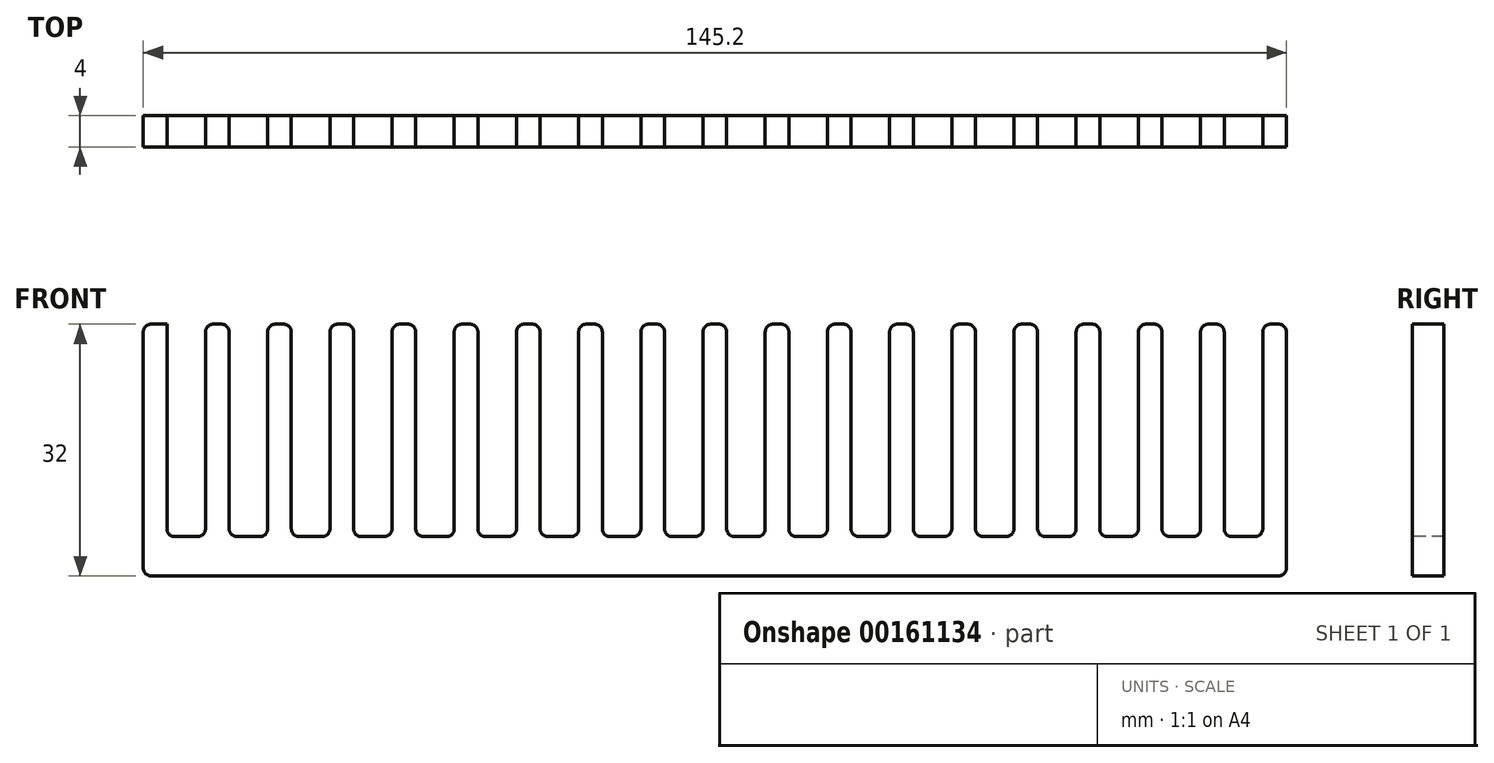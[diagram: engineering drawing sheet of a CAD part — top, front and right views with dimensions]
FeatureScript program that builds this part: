
annotation { "Feature Type Name" : "Feature", "Feature Type Description" : "" }
export const myFeature = defineFeature(function(context is Context, id is Id, definition is map)
    precondition{}
    {
        {
            var Q0;
            Q0=qCreatedBy(makeId("Front.planeOp"),FACE);
            var sketch = newSketch(context, id + "F0", { "sketchPlane" : qUnion([Q0])});
            skLineSegment(sketch, "E0.bottom", {"start": v(2.45, 13.5) * mm, "end": v(-2.45, 13.5) * mm});
            skLineSegment(sketch, "E0.top", {"start": v(1.45, -13.5) * mm, "end": v(-1.45, -13.5) * mm});
            skLineSegment(sketch, "E0.left", {"start": v(2.45, 13.5) * mm, "end": v(2.45, -12.5) * mm});
            skLineSegment(sketch, "E0.right", {"start": v(-2.45, 13.5) * mm, "end": v(-2.45, -12.5) * mm});
            skPoint(sketch, "E0.middle", {"position": v(0, 0) * mm});
            skPoint(sketch, "E1.visualSharp", {"position": v(-2.45, -13.5) * mm});
            skArc(sketch, "E1.filletArc", {"start": v(-2.45, -12.5) * mm, "mid": v(-2.16, -13.2) * mm, "end": v(-1.45, -13.5) * mm});
            skPoint(sketch, "E2.visualSharp", {"position": v(2.45, -13.5) * mm});
            skArc(sketch, "E2.filletArc", {"start": v(1.45, -13.5) * mm, "mid": v(2.16, -13.2) * mm, "end": v(2.45, -12.5) * mm});
            skLineSegment(sketch, "E3.1.0.0", {"start": v(5.45, 13.5) * mm, "end": v(5.45, -12.5) * mm});
            skLineSegment(sketch, "E3.1.0.1", {"start": v(10.35, 13.5) * mm, "end": v(10.35, -12.5) * mm});
            skLineSegment(sketch, "E3.1.0.2", {"start": v(10.35, 13.5) * mm, "end": v(5.45, 13.5) * mm});
            skPoint(sketch, "E3.1.0.3", {"position": v(5.45, -13.5) * mm});
            skPoint(sketch, "E3.1.0.4", {"position": v(7.9, 0) * mm});
            skPoint(sketch, "E3.1.0.5", {"position": v(10.35, -13.5) * mm});
            skLineSegment(sketch, "E3.1.0.6", {"start": v(9.35, -13.5) * mm, "end": v(6.45, -13.5) * mm});
            skArc(sketch, "E3.1.0.7", {"start": v(5.45, -12.5) * mm, "mid": v(5.74, -13.2) * mm, "end": v(6.45, -13.5) * mm});
            skArc(sketch, "E3.1.0.8", {"start": v(9.35, -13.5) * mm, "mid": v(10.06, -13.2) * mm, "end": v(10.35, -12.5) * mm});
            skLineSegment(sketch, "E3.2.0.0", {"start": v(13.35, 13.5) * mm, "end": v(13.35, -12.5) * mm});
            skLineSegment(sketch, "E3.2.0.1", {"start": v(18.25, 13.5) * mm, "end": v(18.25, -12.5) * mm});
            skLineSegment(sketch, "E3.2.0.2", {"start": v(18.25, 13.5) * mm, "end": v(13.35, 13.5) * mm});
            skPoint(sketch, "E3.2.0.3", {"position": v(13.35, -13.5) * mm});
            skPoint(sketch, "E3.2.0.4", {"position": v(15.8, 0) * mm});
            skPoint(sketch, "E3.2.0.5", {"position": v(18.25, -13.5) * mm});
            skLineSegment(sketch, "E3.2.0.6", {"start": v(17.25, -13.5) * mm, "end": v(14.35, -13.5) * mm});
            skArc(sketch, "E3.2.0.7", {"start": v(13.35, -12.5) * mm, "mid": v(13.64, -13.2) * mm, "end": v(14.35, -13.5) * mm});
            skArc(sketch, "E3.2.0.8", {"start": v(17.25, -13.5) * mm, "mid": v(17.96, -13.2) * mm, "end": v(18.25, -12.5) * mm});
            skLineSegment(sketch, "E3.3.0.0", {"start": v(21.25, 13.5) * mm, "end": v(21.25, -12.5) * mm});
            skLineSegment(sketch, "E3.3.0.1", {"start": v(26.15, 13.5) * mm, "end": v(26.15, -12.5) * mm});
            skLineSegment(sketch, "E3.3.0.2", {"start": v(26.15, 13.5) * mm, "end": v(21.25, 13.5) * mm});
            skPoint(sketch, "E3.3.0.3", {"position": v(21.25, -13.5) * mm});
            skPoint(sketch, "E3.3.0.4", {"position": v(23.7, 0) * mm});
            skPoint(sketch, "E3.3.0.5", {"position": v(26.15, -13.5) * mm});
            skLineSegment(sketch, "E3.3.0.6", {"start": v(25.15, -13.5) * mm, "end": v(22.25, -13.5) * mm});
            skArc(sketch, "E3.3.0.7", {"start": v(21.25, -12.5) * mm, "mid": v(21.54, -13.2) * mm, "end": v(22.25, -13.5) * mm});
            skArc(sketch, "E3.3.0.8", {"start": v(25.15, -13.5) * mm, "mid": v(25.86, -13.2) * mm, "end": v(26.15, -12.5) * mm});
            skLineSegment(sketch, "E3.4.0.0", {"start": v(29.15, 13.5) * mm, "end": v(29.15, -12.5) * mm});
            skLineSegment(sketch, "E3.4.0.1", {"start": v(34.05, 13.5) * mm, "end": v(34.05, -12.5) * mm});
            skLineSegment(sketch, "E3.4.0.2", {"start": v(34.05, 13.5) * mm, "end": v(29.15, 13.5) * mm});
            skPoint(sketch, "E3.4.0.3", {"position": v(29.15, -13.5) * mm});
            skPoint(sketch, "E3.4.0.4", {"position": v(31.6, 0) * mm});
            skPoint(sketch, "E3.4.0.5", {"position": v(34.05, -13.5) * mm});
            skLineSegment(sketch, "E3.4.0.6", {"start": v(33.05, -13.5) * mm, "end": v(30.15, -13.5) * mm});
            skArc(sketch, "E3.4.0.7", {"start": v(29.15, -12.5) * mm, "mid": v(29.44, -13.2) * mm, "end": v(30.15, -13.5) * mm});
            skArc(sketch, "E3.4.0.8", {"start": v(33.05, -13.5) * mm, "mid": v(33.76, -13.2) * mm, "end": v(34.05, -12.5) * mm});
            skLineSegment(sketch, "E3.5.0.0", {"start": v(37.05, 13.5) * mm, "end": v(37.05, -12.5) * mm});
            skLineSegment(sketch, "E3.5.0.1", {"start": v(41.95, 13.5) * mm, "end": v(41.95, -12.5) * mm});
            skLineSegment(sketch, "E3.5.0.2", {"start": v(41.95, 13.5) * mm, "end": v(37.05, 13.5) * mm});
            skPoint(sketch, "E3.5.0.3", {"position": v(37.05, -13.5) * mm});
            skPoint(sketch, "E3.5.0.4", {"position": v(39.5, 0) * mm});
            skPoint(sketch, "E3.5.0.5", {"position": v(41.95, -13.5) * mm});
            skLineSegment(sketch, "E3.5.0.6", {"start": v(40.95, -13.5) * mm, "end": v(38.05, -13.5) * mm});
            skArc(sketch, "E3.5.0.7", {"start": v(37.05, -12.5) * mm, "mid": v(37.34, -13.2) * mm, "end": v(38.05, -13.5) * mm});
            skArc(sketch, "E3.5.0.8", {"start": v(40.95, -13.5) * mm, "mid": v(41.66, -13.2) * mm, "end": v(41.95, -12.5) * mm});
            skLineSegment(sketch, "E3.6.0.0", {"start": v(44.95, 13.5) * mm, "end": v(44.95, -12.5) * mm});
            skLineSegment(sketch, "E3.6.0.1", {"start": v(49.85, 13.5) * mm, "end": v(49.85, -12.5) * mm});
            skLineSegment(sketch, "E3.6.0.2", {"start": v(49.85, 13.5) * mm, "end": v(44.95, 13.5) * mm});
            skPoint(sketch, "E3.6.0.3", {"position": v(44.95, -13.5) * mm});
            skPoint(sketch, "E3.6.0.4", {"position": v(47.4, 0) * mm});
            skPoint(sketch, "E3.6.0.5", {"position": v(49.85, -13.5) * mm});
            skLineSegment(sketch, "E3.6.0.6", {"start": v(48.85, -13.5) * mm, "end": v(45.95, -13.5) * mm});
            skArc(sketch, "E3.6.0.7", {"start": v(44.95, -12.5) * mm, "mid": v(45.24, -13.2) * mm, "end": v(45.95, -13.5) * mm});
            skArc(sketch, "E3.6.0.8", {"start": v(48.85, -13.5) * mm, "mid": v(49.56, -13.2) * mm, "end": v(49.85, -12.5) * mm});
            skLineSegment(sketch, "E3.7.0.0", {"start": v(52.85, 13.5) * mm, "end": v(52.85, -12.5) * mm});
            skLineSegment(sketch, "E3.7.0.1", {"start": v(57.75, 13.5) * mm, "end": v(57.75, -12.5) * mm});
            skLineSegment(sketch, "E3.7.0.2", {"start": v(57.75, 13.5) * mm, "end": v(52.85, 13.5) * mm});
            skPoint(sketch, "E3.7.0.3", {"position": v(52.85, -13.5) * mm});
            skPoint(sketch, "E3.7.0.4", {"position": v(55.3, 0) * mm});
            skPoint(sketch, "E3.7.0.5", {"position": v(57.75, -13.5) * mm});
            skLineSegment(sketch, "E3.7.0.6", {"start": v(56.75, -13.5) * mm, "end": v(53.85, -13.5) * mm});
            skArc(sketch, "E3.7.0.7", {"start": v(52.85, -12.5) * mm, "mid": v(53.14, -13.2) * mm, "end": v(53.85, -13.5) * mm});
            skArc(sketch, "E3.7.0.8", {"start": v(56.75, -13.5) * mm, "mid": v(57.46, -13.2) * mm, "end": v(57.75, -12.5) * mm});
            skLineSegment(sketch, "E3.8.0.0", {"start": v(60.75, 13.5) * mm, "end": v(60.75, -12.5) * mm});
            skLineSegment(sketch, "E3.8.0.1", {"start": v(65.65, 13.5) * mm, "end": v(65.65, -12.5) * mm});
            skLineSegment(sketch, "E3.8.0.2", {"start": v(65.65, 13.5) * mm, "end": v(60.75, 13.5) * mm});
            skPoint(sketch, "E3.8.0.3", {"position": v(60.75, -13.5) * mm});
            skPoint(sketch, "E3.8.0.4", {"position": v(63.2, 0) * mm});
            skPoint(sketch, "E3.8.0.5", {"position": v(65.65, -13.5) * mm});
            skLineSegment(sketch, "E3.8.0.6", {"start": v(64.65, -13.5) * mm, "end": v(61.75, -13.5) * mm});
            skArc(sketch, "E3.8.0.7", {"start": v(60.75, -12.5) * mm, "mid": v(61.04, -13.2) * mm, "end": v(61.75, -13.5) * mm});
            skArc(sketch, "E3.8.0.8", {"start": v(64.65, -13.5) * mm, "mid": v(65.36, -13.2) * mm, "end": v(65.65, -12.5) * mm});
            skLineSegment(sketch, "E3.9.0.0", {"start": v(68.65, 13.5) * mm, "end": v(68.65, -12.5) * mm});
            skLineSegment(sketch, "E3.9.0.1", {"start": v(73.55, 13.5) * mm, "end": v(73.55, -12.5) * mm});
            skLineSegment(sketch, "E3.9.0.2", {"start": v(73.55, 13.5) * mm, "end": v(68.65, 13.5) * mm});
            skPoint(sketch, "E3.9.0.3", {"position": v(68.65, -13.5) * mm});
            skPoint(sketch, "E3.9.0.4", {"position": v(71.1, 0) * mm});
            skPoint(sketch, "E3.9.0.5", {"position": v(73.55, -13.5) * mm});
            skLineSegment(sketch, "E3.9.0.6", {"start": v(72.55, -13.5) * mm, "end": v(69.65, -13.5) * mm});
            skArc(sketch, "E3.9.0.7", {"start": v(68.65, -12.5) * mm, "mid": v(68.94, -13.2) * mm, "end": v(69.65, -13.5) * mm});
            skArc(sketch, "E3.9.0.8", {"start": v(72.55, -13.5) * mm, "mid": v(73.26, -13.2) * mm, "end": v(73.55, -12.5) * mm});
            skLineSegment(sketch, "E3.10.0.0", {"start": v(76.55, 13.5) * mm, "end": v(76.55, -12.5) * mm});
            skLineSegment(sketch, "E3.10.0.1", {"start": v(81.45, 13.5) * mm, "end": v(81.45, -12.5) * mm});
            skLineSegment(sketch, "E3.10.0.2", {"start": v(81.45, 13.5) * mm, "end": v(76.55, 13.5) * mm});
            skPoint(sketch, "E3.10.0.3", {"position": v(76.55, -13.5) * mm});
            skPoint(sketch, "E3.10.0.4", {"position": v(79, 0) * mm});
            skPoint(sketch, "E3.10.0.5", {"position": v(81.45, -13.5) * mm});
            skLineSegment(sketch, "E3.10.0.6", {"start": v(80.45, -13.5) * mm, "end": v(77.55, -13.5) * mm});
            skArc(sketch, "E3.10.0.7", {"start": v(76.55, -12.5) * mm, "mid": v(76.84, -13.2) * mm, "end": v(77.55, -13.5) * mm});
            skArc(sketch, "E3.10.0.8", {"start": v(80.45, -13.5) * mm, "mid": v(81.16, -13.2) * mm, "end": v(81.45, -12.5) * mm});
            skLineSegment(sketch, "E3.11.0.0", {"start": v(84.45, 13.5) * mm, "end": v(84.45, -12.5) * mm});
            skLineSegment(sketch, "E3.11.0.1", {"start": v(89.35, 13.5) * mm, "end": v(89.35, -12.5) * mm});
            skLineSegment(sketch, "E3.11.0.2", {"start": v(89.35, 13.5) * mm, "end": v(84.45, 13.5) * mm});
            skPoint(sketch, "E3.11.0.3", {"position": v(84.45, -13.5) * mm});
            skPoint(sketch, "E3.11.0.4", {"position": v(86.9, 0) * mm});
            skPoint(sketch, "E3.11.0.5", {"position": v(89.35, -13.5) * mm});
            skLineSegment(sketch, "E3.11.0.6", {"start": v(88.35, -13.5) * mm, "end": v(85.45, -13.5) * mm});
            skArc(sketch, "E3.11.0.7", {"start": v(84.45, -12.5) * mm, "mid": v(84.74, -13.2) * mm, "end": v(85.45, -13.5) * mm});
            skArc(sketch, "E3.11.0.8", {"start": v(88.35, -13.5) * mm, "mid": v(89.06, -13.2) * mm, "end": v(89.35, -12.5) * mm});
            skLineSegment(sketch, "E3.12.0.0", {"start": v(92.35, 13.5) * mm, "end": v(92.35, -12.5) * mm});
            skLineSegment(sketch, "E3.12.0.1", {"start": v(97.25, 13.5) * mm, "end": v(97.25, -12.5) * mm});
            skLineSegment(sketch, "E3.12.0.2", {"start": v(97.25, 13.5) * mm, "end": v(92.35, 13.5) * mm});
            skPoint(sketch, "E3.12.0.3", {"position": v(92.35, -13.5) * mm});
            skPoint(sketch, "E3.12.0.4", {"position": v(94.8, 0) * mm});
            skPoint(sketch, "E3.12.0.5", {"position": v(97.25, -13.5) * mm});
            skLineSegment(sketch, "E3.12.0.6", {"start": v(96.25, -13.5) * mm, "end": v(93.35, -13.5) * mm});
            skArc(sketch, "E3.12.0.7", {"start": v(92.35, -12.5) * mm, "mid": v(92.64, -13.2) * mm, "end": v(93.35, -13.5) * mm});
            skArc(sketch, "E3.12.0.8", {"start": v(96.25, -13.5) * mm, "mid": v(96.96, -13.2) * mm, "end": v(97.25, -12.5) * mm});
            skLineSegment(sketch, "E3.13.0.0", {"start": v(100.25, 13.5) * mm, "end": v(100.25, -12.5) * mm});
            skLineSegment(sketch, "E3.13.0.1", {"start": v(105.15, 13.5) * mm, "end": v(105.15, -12.5) * mm});
            skLineSegment(sketch, "E3.13.0.2", {"start": v(105.15, 13.5) * mm, "end": v(100.25, 13.5) * mm});
            skPoint(sketch, "E3.13.0.3", {"position": v(100.25, -13.5) * mm});
            skPoint(sketch, "E3.13.0.4", {"position": v(102.7, 0) * mm});
            skPoint(sketch, "E3.13.0.5", {"position": v(105.15, -13.5) * mm});
            skLineSegment(sketch, "E3.13.0.6", {"start": v(104.15, -13.5) * mm, "end": v(101.25, -13.5) * mm});
            skArc(sketch, "E3.13.0.7", {"start": v(100.25, -12.5) * mm, "mid": v(100.54, -13.2) * mm, "end": v(101.25, -13.5) * mm});
            skArc(sketch, "E3.13.0.8", {"start": v(104.15, -13.5) * mm, "mid": v(104.86, -13.2) * mm, "end": v(105.15, -12.5) * mm});
            skLineSegment(sketch, "E3.14.0.0", {"start": v(108.15, 13.5) * mm, "end": v(108.15, -12.5) * mm});
            skLineSegment(sketch, "E3.14.0.1", {"start": v(113.05, 13.5) * mm, "end": v(113.05, -12.5) * mm});
            skLineSegment(sketch, "E3.14.0.2", {"start": v(113.05, 13.5) * mm, "end": v(108.15, 13.5) * mm});
            skPoint(sketch, "E3.14.0.3", {"position": v(108.15, -13.5) * mm});
            skPoint(sketch, "E3.14.0.4", {"position": v(110.6, 0) * mm});
            skPoint(sketch, "E3.14.0.5", {"position": v(113.05, -13.5) * mm});
            skLineSegment(sketch, "E3.14.0.6", {"start": v(112.05, -13.5) * mm, "end": v(109.15, -13.5) * mm});
            skArc(sketch, "E3.14.0.7", {"start": v(108.15, -12.5) * mm, "mid": v(108.44, -13.2) * mm, "end": v(109.15, -13.5) * mm});
            skArc(sketch, "E3.14.0.8", {"start": v(112.05, -13.5) * mm, "mid": v(112.76, -13.2) * mm, "end": v(113.05, -12.5) * mm});
            skLineSegment(sketch, "E3.15.0.0", {"start": v(116.05, 13.5) * mm, "end": v(116.05, -12.5) * mm});
            skLineSegment(sketch, "E3.15.0.1", {"start": v(120.95, 13.5) * mm, "end": v(120.95, -12.5) * mm});
            skLineSegment(sketch, "E3.15.0.2", {"start": v(120.95, 13.5) * mm, "end": v(116.05, 13.5) * mm});
            skPoint(sketch, "E3.15.0.3", {"position": v(116.05, -13.5) * mm});
            skPoint(sketch, "E3.15.0.4", {"position": v(118.5, 0) * mm});
            skPoint(sketch, "E3.15.0.5", {"position": v(120.95, -13.5) * mm});
            skLineSegment(sketch, "E3.15.0.6", {"start": v(119.95, -13.5) * mm, "end": v(117.05, -13.5) * mm});
            skArc(sketch, "E3.15.0.7", {"start": v(116.05, -12.5) * mm, "mid": v(116.34, -13.2) * mm, "end": v(117.05, -13.5) * mm});
            skArc(sketch, "E3.15.0.8", {"start": v(119.95, -13.5) * mm, "mid": v(120.66, -13.2) * mm, "end": v(120.95, -12.5) * mm});
            skLineSegment(sketch, "E3.16.0.0", {"start": v(123.95, 13.5) * mm, "end": v(123.95, -12.5) * mm});
            skLineSegment(sketch, "E3.16.0.1", {"start": v(128.85, 13.5) * mm, "end": v(128.85, -12.5) * mm});
            skLineSegment(sketch, "E3.16.0.2", {"start": v(128.85, 13.5) * mm, "end": v(123.95, 13.5) * mm});
            skPoint(sketch, "E3.16.0.3", {"position": v(123.95, -13.5) * mm});
            skPoint(sketch, "E3.16.0.4", {"position": v(126.4, 0) * mm});
            skPoint(sketch, "E3.16.0.5", {"position": v(128.85, -13.5) * mm});
            skLineSegment(sketch, "E3.16.0.6", {"start": v(127.85, -13.5) * mm, "end": v(124.95, -13.5) * mm});
            skArc(sketch, "E3.16.0.7", {"start": v(123.95, -12.5) * mm, "mid": v(124.24, -13.2) * mm, "end": v(124.95, -13.5) * mm});
            skArc(sketch, "E3.16.0.8", {"start": v(127.85, -13.5) * mm, "mid": v(128.56, -13.2) * mm, "end": v(128.85, -12.5) * mm});
            skLineSegment(sketch, "E3.17.0.0", {"start": v(131.85, 13.5) * mm, "end": v(131.85, -12.5) * mm});
            skLineSegment(sketch, "E3.17.0.1", {"start": v(136.75, 13.5) * mm, "end": v(136.75, -12.5) * mm});
            skLineSegment(sketch, "E3.17.0.2", {"start": v(136.75, 13.5) * mm, "end": v(131.85, 13.5) * mm});
            skPoint(sketch, "E3.17.0.3", {"position": v(131.85, -13.5) * mm});
            skPoint(sketch, "E3.17.0.4", {"position": v(134.3, 0) * mm});
            skPoint(sketch, "E3.17.0.5", {"position": v(136.75, -13.5) * mm});
            skLineSegment(sketch, "E3.17.0.6", {"start": v(135.75, -13.5) * mm, "end": v(132.85, -13.5) * mm});
            skArc(sketch, "E3.17.0.7", {"start": v(131.85, -12.5) * mm, "mid": v(132.14, -13.2) * mm, "end": v(132.85, -13.5) * mm});
            skArc(sketch, "E3.17.0.8", {"start": v(135.75, -13.5) * mm, "mid": v(136.46, -13.2) * mm, "end": v(136.75, -12.5) * mm});
            skLineSegment(sketch, "E3.direction1", {"start": v(-2.45, -13.5) * mm, "end": v(5.45, -13.5) * mm, "construction": true});
            skSolve(sketch);
        }
        {
            var Q0;
            Q0=qCreatedBy(makeId("Front.planeOp"),FACE);
            var sketch = newSketch(context, id + "F1", { "sketchPlane" : qUnion([Q0])});
            skLineSegment(sketch, "E4.bottom", {"start": v(-5.45, 13.5) * mm, "end": v(139.75, 13.5) * mm});
            skLineSegment(sketch, "E4.top", {"start": v(-5.45, -18.5) * mm, "end": v(139.75, -18.5) * mm});
            skLineSegment(sketch, "E4.left", {"start": v(-5.45, 13.5) * mm, "end": v(-5.45, -18.5) * mm});
            skLineSegment(sketch, "E4.right", {"start": v(139.75, 13.5) * mm, "end": v(139.75, -18.5) * mm});
            skSolve(sketch);
        }
        {
            var Q0;
            Q0 = qSketchRegion(id + "F1", true);
            extrude(context, id + "F2", {"entities" : qUnion([Q0]), "endBound" : BoundingType.SYMMETRIC, "depth" : 4 * mm});
        }
        {
            var Q0;
            Q0 = qSketchRegion(id + "F0", true);
            extrude(context, id + "F3", {"entities" : qUnion([Q0]), "operationType" : NewBodyOperationType.REMOVE, "endBound" : BoundingType.THROUGH_ALL, "oppositeDirection" : true, "depth" : 25 * mm, "hasSecondDirection" : true, "secondDirectionBound" : SecondDirectionBoundingType.THROUGH_ALL, "secondDirectionOppositeDirection" : false, "secondDirectionDepth" : 25 * mm});
        }
        {
            var Q0;
            Q0=makeQuery(id+"F2.opExtrude","SWEPT_EDGE",EDGE,{"disambiguationData":[OSD([sQuery(id+"F1.wireOp",EDGE,"E4.bottom"),sQuery(id+"F1.wireOp",EDGE,"E4.left")])]});
            var Q1;
            Q1=makeQuery(id+"F2.opExtrude","SWEPT_EDGE",EDGE,{"disambiguationData":[OSD([sQuery(id+"F1.wireOp",EDGE,"E4.bottom"),sQuery(id+"F1.wireOp",EDGE,"E4.right")])]});
            var Q2;
            Q2=makeQuery(id+"F2.opExtrude","SWEPT_EDGE",EDGE,{"disambiguationData":[OSD([sQuery(id+"F1.wireOp",EDGE,"E4.top"),sQuery(id+"F1.wireOp",EDGE,"E4.right")])]});
            var Q3;
            Q3=makeQuery(id+"F2.opExtrude","SWEPT_EDGE",EDGE,{"disambiguationData":[OSD([sQuery(id+"F1.wireOp",EDGE,"E4.top"),sQuery(id+"F1.wireOp",EDGE,"E4.left")])]});
            var Q4;
            Q4=makeQuery(id+"F3.boolean.opBoolean","COPY",EDGE,{"derivedFrom":makeQuery(id+"F3.opExtrude","SWEPT_EDGE",EDGE,{"disambiguationData":[OSD([sQuery(id+"F0.wireOp",EDGE,"E0.bottom"),sQuery(id+"F0.wireOp",EDGE,"E0.right")])]})});
            var Q5;
            Q5=makeQuery(id+"F3.boolean.opBoolean","COPY",EDGE,{"derivedFrom":makeQuery(id+"F3.opExtrude","SWEPT_EDGE",EDGE,{"disambiguationData":[OSD([sQuery(id+"F0.wireOp",EDGE,"E3.1.0.0"),sQuery(id+"F0.wireOp",EDGE,"E3.1.0.2")])]})});
            var Q6;
            Q6=makeQuery(id+"F3.boolean.opBoolean","COPY",EDGE,{"derivedFrom":makeQuery(id+"F3.opExtrude","SWEPT_EDGE",EDGE,{"disambiguationData":[OSD([sQuery(id+"F0.wireOp",EDGE,"E3.2.0.0"),sQuery(id+"F0.wireOp",EDGE,"E3.2.0.2")])]})});
            var Q7;
            Q7=makeQuery(id+"F3.boolean.opBoolean","COPY",EDGE,{"derivedFrom":makeQuery(id+"F3.opExtrude","SWEPT_EDGE",EDGE,{"disambiguationData":[OSD([sQuery(id+"F0.wireOp",EDGE,"E0.bottom"),sQuery(id+"F0.wireOp",EDGE,"E0.left")])]})});
            var Q8;
            Q8=makeQuery(id+"F3.boolean.opBoolean","COPY",EDGE,{"derivedFrom":makeQuery(id+"F3.opExtrude","SWEPT_EDGE",EDGE,{"disambiguationData":[OSD([sQuery(id+"F0.wireOp",EDGE,"E3.2.0.1"),sQuery(id+"F0.wireOp",EDGE,"E3.2.0.2")])]})});
            var Q9;
            Q9=makeQuery(id+"F3.boolean.opBoolean","COPY",EDGE,{"derivedFrom":makeQuery(id+"F3.opExtrude","SWEPT_EDGE",EDGE,{"disambiguationData":[OSD([sQuery(id+"F0.wireOp",EDGE,"E3.3.0.1"),sQuery(id+"F0.wireOp",EDGE,"E3.3.0.2")])]})});
            var Q10;
            Q10=makeQuery(id+"F3.boolean.opBoolean","COPY",EDGE,{"derivedFrom":makeQuery(id+"F3.opExtrude","SWEPT_EDGE",EDGE,{"disambiguationData":[OSD([sQuery(id+"F0.wireOp",EDGE,"E3.1.0.1"),sQuery(id+"F0.wireOp",EDGE,"E3.1.0.2")])]})});
            var Q11;
            Q11=makeQuery(id+"F3.boolean.opBoolean","COPY",EDGE,{"derivedFrom":makeQuery(id+"F3.opExtrude","SWEPT_EDGE",EDGE,{"disambiguationData":[OSD([sQuery(id+"F0.wireOp",EDGE,"E3.3.0.0"),sQuery(id+"F0.wireOp",EDGE,"E3.3.0.2")])]})});
            var Q12;
            Q12=makeQuery(id+"F3.boolean.opBoolean","COPY",EDGE,{"derivedFrom":makeQuery(id+"F3.opExtrude","SWEPT_EDGE",EDGE,{"disambiguationData":[OSD([sQuery(id+"F0.wireOp",EDGE,"E3.4.0.0"),sQuery(id+"F0.wireOp",EDGE,"E3.4.0.2")])]})});
            var Q13;
            Q13=makeQuery(id+"F3.boolean.opBoolean","COPY",EDGE,{"derivedFrom":makeQuery(id+"F3.opExtrude","SWEPT_EDGE",EDGE,{"disambiguationData":[OSD([sQuery(id+"F0.wireOp",EDGE,"E3.4.0.1"),sQuery(id+"F0.wireOp",EDGE,"E3.4.0.2")])]})});
            var Q14;
            Q14=makeQuery(id+"F3.boolean.opBoolean","COPY",EDGE,{"derivedFrom":makeQuery(id+"F3.opExtrude","SWEPT_EDGE",EDGE,{"disambiguationData":[OSD([sQuery(id+"F0.wireOp",EDGE,"E3.5.0.0"),sQuery(id+"F0.wireOp",EDGE,"E3.5.0.2")])]})});
            var Q15;
            Q15=makeQuery(id+"F3.boolean.opBoolean","COPY",EDGE,{"derivedFrom":makeQuery(id+"F3.opExtrude","SWEPT_EDGE",EDGE,{"disambiguationData":[OSD([sQuery(id+"F0.wireOp",EDGE,"E3.5.0.1"),sQuery(id+"F0.wireOp",EDGE,"E3.5.0.2")])]})});
            var Q16;
            Q16=makeQuery(id+"F3.boolean.opBoolean","COPY",EDGE,{"derivedFrom":makeQuery(id+"F3.opExtrude","SWEPT_EDGE",EDGE,{"disambiguationData":[OSD([sQuery(id+"F0.wireOp",EDGE,"E3.6.0.0"),sQuery(id+"F0.wireOp",EDGE,"E3.6.0.2")])]})});
            var Q17;
            Q17=makeQuery(id+"F3.boolean.opBoolean","COPY",EDGE,{"derivedFrom":makeQuery(id+"F3.opExtrude","SWEPT_EDGE",EDGE,{"disambiguationData":[OSD([sQuery(id+"F0.wireOp",EDGE,"E3.6.0.1"),sQuery(id+"F0.wireOp",EDGE,"E3.6.0.2")])]})});
            var Q18;
            Q18=makeQuery(id+"F3.boolean.opBoolean","COPY",EDGE,{"derivedFrom":makeQuery(id+"F3.opExtrude","SWEPT_EDGE",EDGE,{"disambiguationData":[OSD([sQuery(id+"F0.wireOp",EDGE,"E3.7.0.0"),sQuery(id+"F0.wireOp",EDGE,"E3.7.0.2")])]})});
            var Q19;
            Q19=makeQuery(id+"F3.boolean.opBoolean","COPY",EDGE,{"derivedFrom":makeQuery(id+"F3.opExtrude","SWEPT_EDGE",EDGE,{"disambiguationData":[OSD([sQuery(id+"F0.wireOp",EDGE,"E3.8.0.0"),sQuery(id+"F0.wireOp",EDGE,"E3.8.0.2")])]})});
            var Q20;
            Q20=makeQuery(id+"F3.boolean.opBoolean","COPY",EDGE,{"derivedFrom":makeQuery(id+"F3.opExtrude","SWEPT_EDGE",EDGE,{"disambiguationData":[OSD([sQuery(id+"F0.wireOp",EDGE,"E3.7.0.1"),sQuery(id+"F0.wireOp",EDGE,"E3.7.0.2")])]})});
            var Q21;
            Q21=makeQuery(id+"F3.boolean.opBoolean","COPY",EDGE,{"derivedFrom":makeQuery(id+"F3.opExtrude","SWEPT_EDGE",EDGE,{"disambiguationData":[OSD([sQuery(id+"F0.wireOp",EDGE,"E3.8.0.1"),sQuery(id+"F0.wireOp",EDGE,"E3.8.0.2")])]})});
            var Q22;
            Q22=makeQuery(id+"F3.boolean.opBoolean","COPY",EDGE,{"derivedFrom":makeQuery(id+"F3.opExtrude","SWEPT_EDGE",EDGE,{"disambiguationData":[OSD([sQuery(id+"F0.wireOp",EDGE,"E3.9.0.0"),sQuery(id+"F0.wireOp",EDGE,"E3.9.0.2")])]})});
            var Q23;
            Q23=makeQuery(id+"F3.boolean.opBoolean","COPY",EDGE,{"derivedFrom":makeQuery(id+"F3.opExtrude","SWEPT_EDGE",EDGE,{"disambiguationData":[OSD([sQuery(id+"F0.wireOp",EDGE,"E3.9.0.1"),sQuery(id+"F0.wireOp",EDGE,"E3.9.0.2")])]})});
            var Q24;
            Q24=makeQuery(id+"F3.boolean.opBoolean","COPY",EDGE,{"derivedFrom":makeQuery(id+"F3.opExtrude","SWEPT_EDGE",EDGE,{"disambiguationData":[OSD([sQuery(id+"F0.wireOp",EDGE,"E3.10.0.0"),sQuery(id+"F0.wireOp",EDGE,"E3.10.0.2")])]})});
            var Q25;
            Q25=makeQuery(id+"F3.boolean.opBoolean","COPY",EDGE,{"derivedFrom":makeQuery(id+"F3.opExtrude","SWEPT_EDGE",EDGE,{"disambiguationData":[OSD([sQuery(id+"F0.wireOp",EDGE,"E3.10.0.1"),sQuery(id+"F0.wireOp",EDGE,"E3.10.0.2")])]})});
            var Q26;
            Q26=makeQuery(id+"F3.boolean.opBoolean","COPY",EDGE,{"derivedFrom":makeQuery(id+"F3.opExtrude","SWEPT_EDGE",EDGE,{"disambiguationData":[OSD([sQuery(id+"F0.wireOp",EDGE,"E3.11.0.0"),sQuery(id+"F0.wireOp",EDGE,"E3.11.0.2")])]})});
            var Q27;
            Q27=makeQuery(id+"F3.boolean.opBoolean","COPY",EDGE,{"derivedFrom":makeQuery(id+"F3.opExtrude","SWEPT_EDGE",EDGE,{"disambiguationData":[OSD([sQuery(id+"F0.wireOp",EDGE,"E3.11.0.1"),sQuery(id+"F0.wireOp",EDGE,"E3.11.0.2")])]})});
            var Q28;
            Q28=makeQuery(id+"F3.boolean.opBoolean","COPY",EDGE,{"derivedFrom":makeQuery(id+"F3.opExtrude","SWEPT_EDGE",EDGE,{"disambiguationData":[OSD([sQuery(id+"F0.wireOp",EDGE,"E3.12.0.0"),sQuery(id+"F0.wireOp",EDGE,"E3.12.0.2")])]})});
            var Q29;
            Q29=makeQuery(id+"F3.boolean.opBoolean","COPY",EDGE,{"derivedFrom":makeQuery(id+"F3.opExtrude","SWEPT_EDGE",EDGE,{"disambiguationData":[OSD([sQuery(id+"F0.wireOp",EDGE,"E3.12.0.1"),sQuery(id+"F0.wireOp",EDGE,"E3.12.0.2")])]})});
            var Q30;
            Q30=makeQuery(id+"F3.boolean.opBoolean","COPY",EDGE,{"derivedFrom":makeQuery(id+"F3.opExtrude","SWEPT_EDGE",EDGE,{"disambiguationData":[OSD([sQuery(id+"F0.wireOp",EDGE,"E3.13.0.0"),sQuery(id+"F0.wireOp",EDGE,"E3.13.0.2")])]})});
            var Q31;
            Q31=makeQuery(id+"F3.boolean.opBoolean","COPY",EDGE,{"derivedFrom":makeQuery(id+"F3.opExtrude","SWEPT_EDGE",EDGE,{"disambiguationData":[OSD([sQuery(id+"F0.wireOp",EDGE,"E3.13.0.1"),sQuery(id+"F0.wireOp",EDGE,"E3.13.0.2")])]})});
            var Q32;
            Q32=makeQuery(id+"F3.boolean.opBoolean","COPY",EDGE,{"derivedFrom":makeQuery(id+"F3.opExtrude","SWEPT_EDGE",EDGE,{"disambiguationData":[OSD([sQuery(id+"F0.wireOp",EDGE,"E3.14.0.0"),sQuery(id+"F0.wireOp",EDGE,"E3.14.0.2")])]})});
            var Q33;
            Q33=makeQuery(id+"F3.boolean.opBoolean","COPY",EDGE,{"derivedFrom":makeQuery(id+"F3.opExtrude","SWEPT_EDGE",EDGE,{"disambiguationData":[OSD([sQuery(id+"F0.wireOp",EDGE,"E3.14.0.1"),sQuery(id+"F0.wireOp",EDGE,"E3.14.0.2")])]})});
            var Q34;
            Q34=makeQuery(id+"F3.boolean.opBoolean","COPY",EDGE,{"derivedFrom":makeQuery(id+"F3.opExtrude","SWEPT_EDGE",EDGE,{"disambiguationData":[OSD([sQuery(id+"F0.wireOp",EDGE,"E3.15.0.0"),sQuery(id+"F0.wireOp",EDGE,"E3.15.0.2")])]})});
            var Q35;
            Q35=makeQuery(id+"F3.boolean.opBoolean","COPY",EDGE,{"derivedFrom":makeQuery(id+"F3.opExtrude","SWEPT_EDGE",EDGE,{"disambiguationData":[OSD([sQuery(id+"F0.wireOp",EDGE,"E3.15.0.1"),sQuery(id+"F0.wireOp",EDGE,"E3.15.0.2")])]})});
            var Q36;
            Q36=makeQuery(id+"F3.boolean.opBoolean","COPY",EDGE,{"derivedFrom":makeQuery(id+"F3.opExtrude","SWEPT_EDGE",EDGE,{"disambiguationData":[OSD([sQuery(id+"F0.wireOp",EDGE,"E3.16.0.0"),sQuery(id+"F0.wireOp",EDGE,"E3.16.0.2")])]})});
            var Q37;
            Q37=makeQuery(id+"F3.boolean.opBoolean","COPY",EDGE,{"derivedFrom":makeQuery(id+"F3.opExtrude","SWEPT_EDGE",EDGE,{"disambiguationData":[OSD([sQuery(id+"F0.wireOp",EDGE,"E3.16.0.1"),sQuery(id+"F0.wireOp",EDGE,"E3.16.0.2")])]})});
            var Q38;
            Q38=makeQuery(id+"F3.boolean.opBoolean","COPY",EDGE,{"derivedFrom":makeQuery(id+"F3.opExtrude","SWEPT_EDGE",EDGE,{"disambiguationData":[OSD([sQuery(id+"F0.wireOp",EDGE,"E3.17.0.0"),sQuery(id+"F0.wireOp",EDGE,"E3.17.0.2")])]})});
            var Q39;
            Q39=makeQuery(id+"F3.boolean.opBoolean","COPY",EDGE,{"derivedFrom":makeQuery(id+"F3.opExtrude","SWEPT_EDGE",EDGE,{"disambiguationData":[OSD([sQuery(id+"F0.wireOp",EDGE,"E3.17.0.1"),sQuery(id+"F0.wireOp",EDGE,"E3.17.0.2")])]})});
            fillet(context, id + "F4", {"entities" : qUnion([Q0, Q1, Q2, Q3, Q4, Q5, Q6, Q7, Q8, Q9, Q10, Q11, Q12, Q13, Q14, Q15, Q16, Q17, Q18, Q19, Q20, Q21, Q22, Q23, Q24, Q25, Q26, Q27, Q28, Q29, Q30, Q31, Q32, Q33, Q34, Q35, Q36, Q37, Q38, Q39]), "radius" : 1 * mm, "tangentPropagation" : true, "allowEdgeOverflow" : false});
        }
    });
